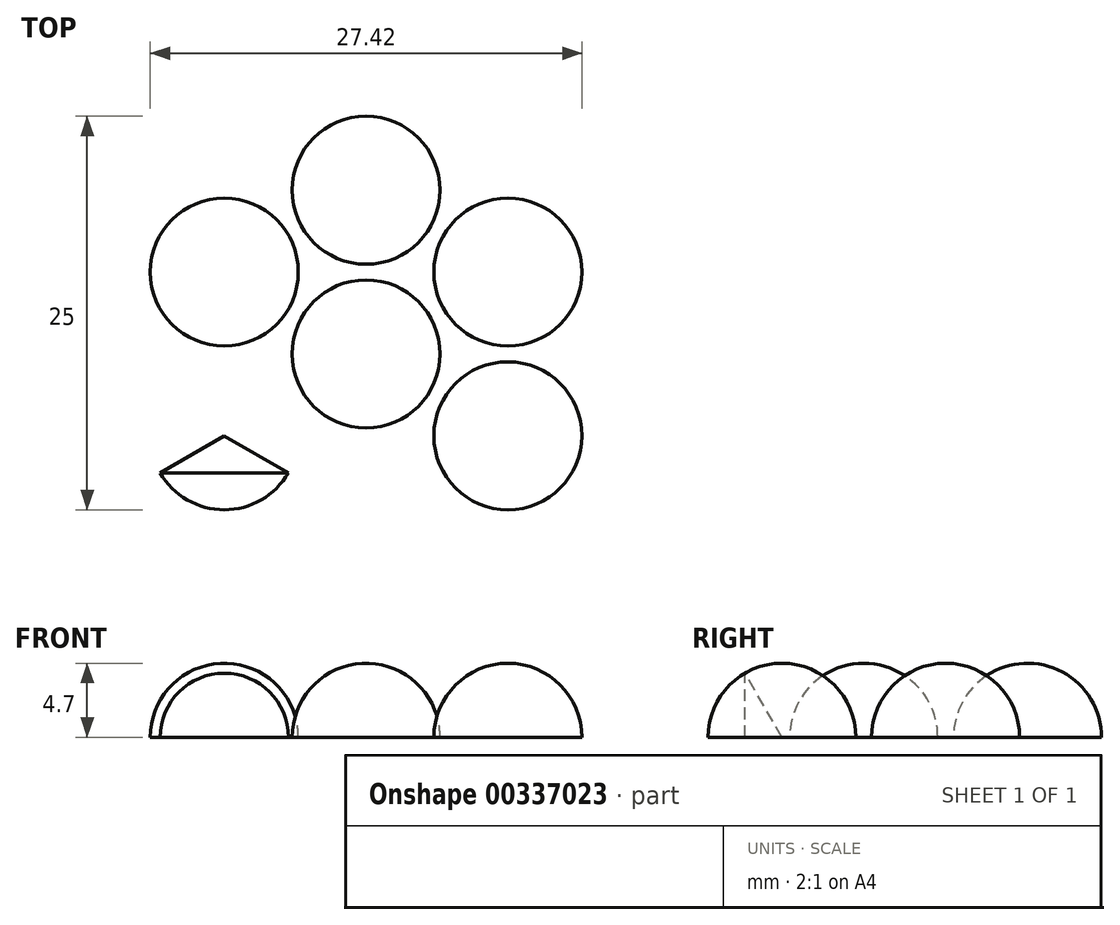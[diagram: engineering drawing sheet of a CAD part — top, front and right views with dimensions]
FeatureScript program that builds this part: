
annotation { "Feature Type Name" : "Feature", "Feature Type Description" : "" }
export const myFeature = defineFeature(function(context is Context, id is Id, definition is map)
    precondition{}
    {
        {
            var Q0;
            Q0=qCreatedBy(makeId("Top.planeOp"),FACE);
            var sketch = newSketch(context, id + "F0", { "sketchPlane" : qUnion([Q0])});
            skLineSegment(sketch, "E0", {"start": v(0, 4.7) * mm, "end": v(0, -4.7) * mm});
            skArc(sketch, "E1", {"start": v(0, 4.7) * mm, "mid": v(-4.7, 0) * mm, "end": v(0, -4.7) * mm});
            skSolve(sketch);
        }
        {
            var Q0;
            Q0 = qSketchRegion(id + "F0", true);
            var Q1;
            Q1=sQuery(id+"F0.wireOp",EDGE,"E0");
            revolve(context, id + "F1", {"entities" : qUnion([Q0]), "axis" : qUnion([Q1]), "revolveType" : RevolveType.ONE_DIRECTION, "oppositeDirection" : true, "angle" : 180 * degree});
        }
        {
            var Q0;
            Q0=qCreatedBy(makeId("Top.planeOp"),FACE);
            var sketch = newSketch(context, id + "F2", { "sketchPlane" : qUnion([Q0])});
            skLineSegment(sketch, "E2", {"start": v(0, 0) * mm, "end": v(0, 10.4) * mm, "construction": true});
            skLineSegment(sketch, "E3", {"start": v(0, 0) * mm, "end": v(10.4, 0) * mm, "construction": true});
            skLineSegment(sketch, "E4", {"start": v(0, 0) * mm, "end": v(9, 5.2) * mm, "construction": true});
            skLineSegment(sketch, "E5", {"start": v(0, 15.1) * mm, "end": v(0, 5.7) * mm});
            skArc(sketch, "E6", {"start": v(0, 5.7) * mm, "mid": v(4.7, 10.4) * mm, "end": v(0, 15.1) * mm});
            skArc(sketch, "E7.MirrorCS", {"start": v(4.94, -2.85) * mm, "mid": v(11.36, -1.13) * mm, "end": v(13.08, -7.55) * mm});
            skLineSegment(sketch, "E8.MirrorCS", {"start": v(13.08, -7.55) * mm, "end": v(4.94, -2.85) * mm});
            skArc(sketch, "E9.MirrorCS", {"start": v(0, -5.7) * mm, "mid": v(4.7, -10.4) * mm, "end": v(0, -15.1) * mm});
            skLineSegment(sketch, "E10.MirrorCS", {"start": v(0, -15.1) * mm, "end": v(0, -5.7) * mm});
            skArc(sketch, "E11.MirrorCS", {"start": v(-4.94, -2.85) * mm, "mid": v(-11.36, -1.13) * mm, "end": v(-13.08, -7.55) * mm});
            skLineSegment(sketch, "E12.MirrorCS", {"start": v(-13.08, -7.55) * mm, "end": v(-4.94, -2.85) * mm});
            skLineSegment(sketch, "E13", {"start": v(9, 9.9) * mm, "end": v(9, 0.5) * mm});
            skArc(sketch, "E14", {"start": v(9, 0.5) * mm, "mid": v(13.7, 5.2) * mm, "end": v(9, 9.9) * mm});
            skLineSegment(sketch, "E15.MirrorCS", {"start": v(-9, 9.9) * mm, "end": v(-9, 0.5) * mm});
            skArc(sketch, "E16.MirrorCS", {"start": v(-9, 0.5) * mm, "mid": v(-13.7, 5.2) * mm, "end": v(-9, 9.9) * mm});
            skArc(sketch, "E17.MirrorCS", {"start": v(-9, -0.5) * mm, "mid": v(-13.7, -5.2) * mm, "end": v(-9, -9.9) * mm});
            skLineSegment(sketch, "E18.MirrorCS", {"start": v(-9, -9.9) * mm, "end": v(-9, -0.5) * mm});
            skLineSegment(sketch, "E19.MirrorCS", {"start": v(9, -9.9) * mm, "end": v(9, -0.5) * mm});
            skArc(sketch, "E20.MirrorCS", {"start": v(9, -0.5) * mm, "mid": v(13.7, -5.2) * mm, "end": v(9, -9.9) * mm});
            skSolve(sketch);
        }
        {
            var Q0;
            Q0=makeQuery(id+"F2.imprint","IMPRINT",FACE,{"disambiguationData":[TD([[makeQuery(id+"F2.imprint","IMPRINT",EDGE,{"derivedFrom":sQuery(id+"F2.wireOp",EDGE,"E5")}),1.0]])]});
            var Q1;
            Q1=makeQuery(id+"F2.imprint","IMPRINT",FACE,{"disambiguationData":[TD([[makeQuery(id+"F2.imprint","IMPRINT",EDGE,{"derivedFrom":sQuery(id+"F2.wireOp",EDGE,"E9.MirrorCS")}),-1.0]])]});
            var Q2;
            Q2=sQuery(id+"F2.wireOp",EDGE,"E5");
            revolve(context, id + "F3", {"operationType" : NewBodyOperationType.ADD, "entities" : qUnion([Q0, Q1]), "axis" : qUnion([Q2]), "revolveType" : RevolveType.ONE_DIRECTION, "angle" : 180 * degree});
        }
        {
            var Q0;
            Q0=makeQuery(id+"F2.imprint","IMPRINT",FACE,{"disambiguationData":[TD([[makeQuery(id+"F2.imprint","IMPRINT",EDGE,{"derivedFrom":sQuery(id+"F2.wireOp",EDGE,"E15.MirrorCS")}),-1.0]])]});
            var Q1;
            Q1=makeQuery(id+"F2.imprint","IMPRINT",FACE,{"disambiguationData":[TD([[makeQuery(id+"F2.imprint","IMPRINT",EDGE,{"derivedFrom":sQuery(id+"F2.wireOp",EDGE,"E17.MirrorCS")}),1.0]])]});
            var Q2;
            Q2=sQuery(id+"F2.wireOp",EDGE,"E15.MirrorCS");
            revolve(context, id + "F4", {"entities" : qUnion([Q0, Q1]), "axis" : qUnion([Q2]), "revolveType" : RevolveType.ONE_DIRECTION, "oppositeDirection" : true, "angle" : 180 * degree});
        }
        {
            var Q0;
            Q0=makeQuery(id+"F2.imprint","IMPRINT",FACE,{"disambiguationData":[TD([[makeQuery(id+"F2.imprint","IMPRINT",EDGE,{"derivedFrom":sQuery(id+"F2.wireOp",EDGE,"E13")}),1.0]])]});
            var Q1;
            Q1=makeQuery(id+"F2.imprint","IMPRINT",FACE,{"disambiguationData":[TD([[makeQuery(id+"F2.imprint","IMPRINT",EDGE,{"derivedFrom":sQuery(id+"F2.wireOp",EDGE,"E19.MirrorCS")}),-1.0]])]});
            var Q2;
            Q2=sQuery(id+"F2.wireOp",EDGE,"E13");
            revolve(context, id + "F5", {"entities" : qUnion([Q0, Q1]), "axis" : qUnion([Q2]), "revolveType" : RevolveType.ONE_DIRECTION, "angle" : 180 * degree});
        }
    });
